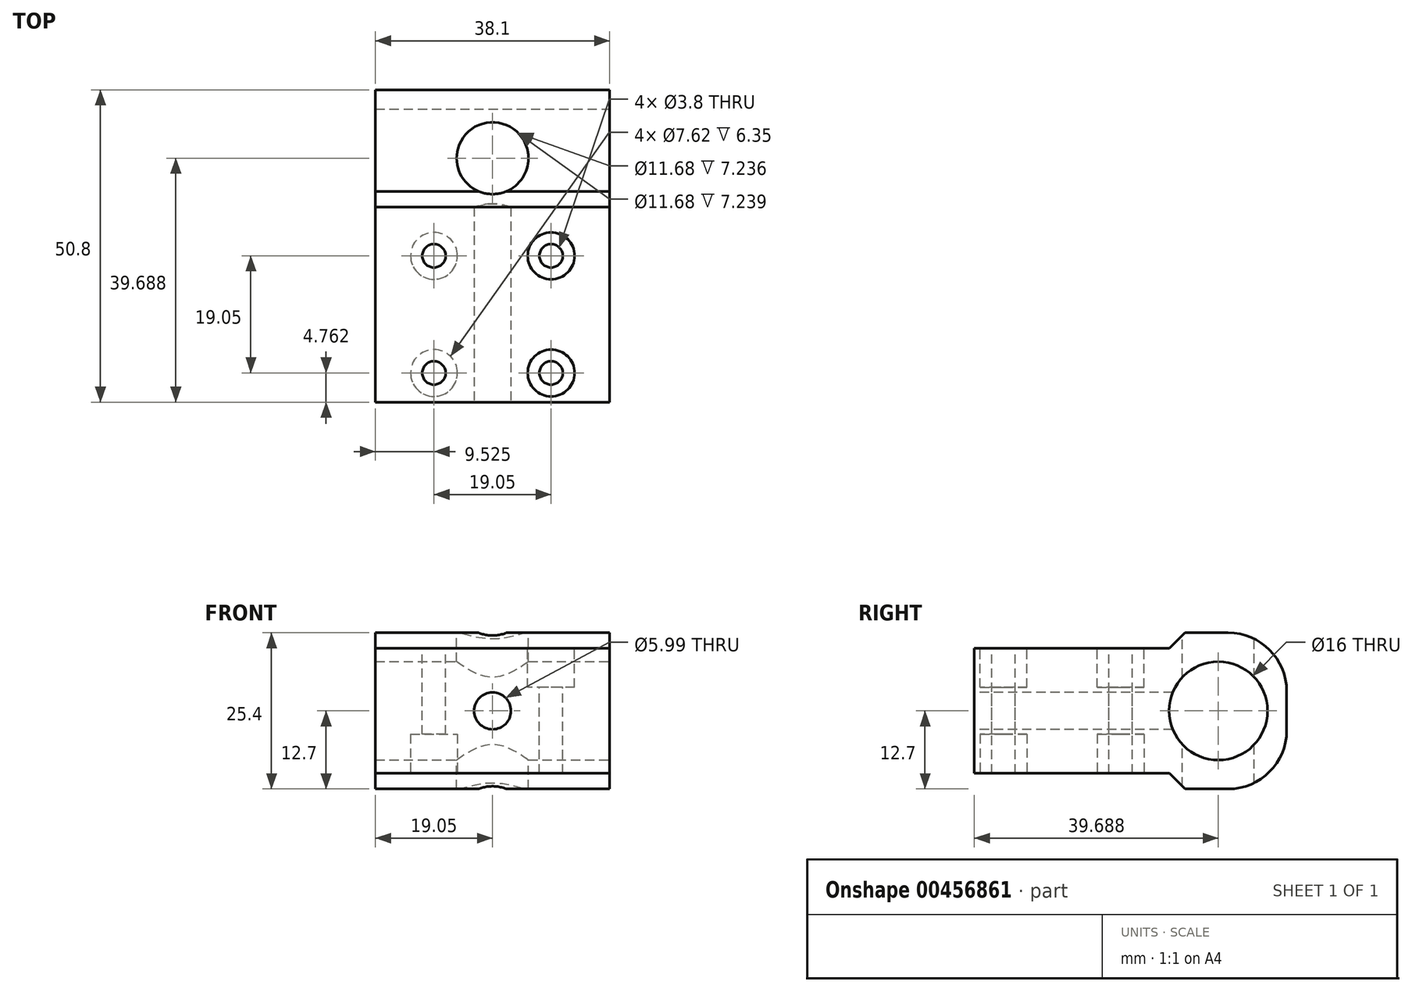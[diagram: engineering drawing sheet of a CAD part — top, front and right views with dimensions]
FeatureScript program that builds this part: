
annotation { "Feature Type Name" : "Feature", "Feature Type Description" : "" }
export const myFeature = defineFeature(function(context is Context, id is Id, definition is map)
    precondition{}
    {
        {
            var Q0;
            Q0=qCreatedBy(makeId("Top.planeOp"),FACE);
            var sketch = newSketch(context, id + "F0", { "sketchPlane" : qUnion([Q0])});
            skLineSegment(sketch, "E0.bottom", {"start": v(19.05, -25.4) * mm, "end": v(-19.05, -25.4) * mm});
            skLineSegment(sketch, "E0.top", {"start": v(19.05, 25.4) * mm, "end": v(-19.05, 25.4) * mm});
            skLineSegment(sketch, "E0.left", {"start": v(19.05, -25.4) * mm, "end": v(19.05, 25.4) * mm});
            skLineSegment(sketch, "E0.right", {"start": v(-19.05, -25.4) * mm, "end": v(-19.05, 25.4) * mm});
            skPoint(sketch, "E0.middle", {"position": v(0, 0) * mm});
            skSolve(sketch);
        }
        {
            var Q0;
            Q0 = qSketchRegion(id + "F0", true);
            extrude(context, id + "F1", {"entities" : qUnion([Q0]), "depth" : 25.4 * mm});
        }
        {
            var Q0;
            Q0=makeQuery(id+"F1.opExtrude","SWEPT_FACE",FACE,{"disambiguationData":[OSD([sQuery(id+"F0.wireOp",EDGE,"E0.left")])]});
            var sketch = newSketch(context, id + "F2", { "sketchPlane" : qUnion([Q0])});
            skCircle(sketch, "E1", {"center": v(14.29, 12.7) * mm, "radius": 8 * mm});
            skPoint(sketch, "E1.centerSnap0", {"position": v(25.4, 12.7) * mm});
            skSolve(sketch);
        }
        {
            var Q0;
            Q0 = qSketchRegion(id + "F2", true);
            extrude(context, id + "F3", {"entities" : qUnion([Q0]), "operationType" : NewBodyOperationType.REMOVE, "endBound" : BoundingType.THROUGH_ALL, "oppositeDirection" : true, "depth" : 25.4 * mm});
        }
        {
            var Q0;
            Q0=makeQuery(id+"F1.opExtrude","SWEPT_FACE",FACE,{"disambiguationData":[OSD([sQuery(id+"F0.wireOp",EDGE,"E0.bottom")])]});
            var sketch = newSketch(context, id + "F4", { "sketchPlane" : qUnion([Q0])});
            skCircle(sketch, "E2", {"center": v(0, 12.7) * mm, "radius": 3 * mm});
            skPoint(sketch, "E2.centerSnap0", {"position": v(19.05, 12.7) * mm});
            skSolve(sketch);
        }
        {
            var Q0;
            Q0 = qSketchRegion(id + "F4", true);
            extrude(context, id + "F5", {"entities" : qUnion([Q0]), "operationType" : NewBodyOperationType.REMOVE, "endBound" : BoundingType.UP_TO_NEXT, "oppositeDirection" : true, "depth" : 25.4 * mm});
        }
        {
            var Q0;
            Q0=makeQuery(id+"F1.opExtrude","CAP_EDGE",EDGE,{"disambiguationData":[OSD([sQuery(id+"F0.wireOp",EDGE,"E0.top")])],"isStart":false});
            var Q1;
            Q1=makeQuery(id+"F1.opExtrude","CAP_EDGE",EDGE,{"disambiguationData":[OSD([sQuery(id+"F0.wireOp",EDGE,"E0.top")])],"isStart":true});
            fillet(context, id + "F6", {"entities" : qUnion([Q0, Q1]), "radius" : 9.52 * mm, "tangentPropagation" : true, "allowEdgeOverflow" : false});
        }
        {
            var Q0;
            Q0=makeQuery(id+"F1.opExtrude","CAP_FACE",FACE,{"disambiguationData":[OSD([sQuery(id+"F0.wireOp",EDGE,"E0.bottom"),sQuery(id+"F0.wireOp",EDGE,"E0.top"),sQuery(id+"F0.wireOp",EDGE,"E0.left"),sQuery(id+"F0.wireOp",EDGE,"E0.right")])],"isStart":false});
            var sketch = newSketch(context, id + "F7", { "sketchPlane" : qUnion([Q0])});
            skPoint(sketch, "E3", {"position": v(-9.53, -20.64) * mm});
            skPoint(sketch, "E4", {"position": v(-9.53, -1.59) * mm});
            skPoint(sketch, "E5", {"position": v(9.52, -1.59) * mm});
            skPoint(sketch, "E6", {"position": v(9.52, -20.64) * mm});
            skSolve(sketch);
        }
        {
            var Q0;
            Q0=sQuery(id+"F7.wireOp",VERTEX,"E4");
            var Q1;
            Q1=sQuery(id+"F7.wireOp",VERTEX,"E3");
            var Q2;
            Q2=sQuery(id+"F7.wireOp",VERTEX,"E6");
            var Q3;
            Q3=sQuery(id+"F7.wireOp",VERTEX,"E5");
            var Q4;
            Q4=makeQuery(id+"F1.opExtrude","SWEPT_BODY",BODY,{"disambiguationData":[OSD([sQuery(id+"F0.wireOp",EDGE,"E0.bottom"),sQuery(id+"F0.wireOp",EDGE,"E0.top"),sQuery(id+"F0.wireOp",EDGE,"E0.left"),sQuery(id+"F0.wireOp",EDGE,"E0.right")])]});
            hole(context, id + "F8", {"style" : HoleStyle.C_SINK, "endStyle" : HoleEndStyle.THROUGH, "holeDiameter" : 3.8 * mm, "cSinkDiameter" : 4.32 * mm, "cSinkAngle" : 90 * degree, "isTappedThrough" : true, "tappedDepth" : 12.7 * mm, "tapClearance" : 3, "startFromSketch" : true, "locations" : qUnion([Q0, Q1, Q2, Q3]), "scope" : qUnion([Q4])});
        }
        {
            var Q0;
            Q0=makeQuery(id+"F1.opExtrude","CAP_FACE",FACE,{"disambiguationData":[OSD([sQuery(id+"F0.wireOp",EDGE,"E0.bottom"),sQuery(id+"F0.wireOp",EDGE,"E0.top"),sQuery(id+"F0.wireOp",EDGE,"E0.left"),sQuery(id+"F0.wireOp",EDGE,"E0.right")])],"isStart":false});
            var sketch = newSketch(context, id + "F9", { "sketchPlane" : qUnion([Q0])});
            skCircle(sketch, "E7", {"center": v(9.52, -1.59) * mm, "radius": 3.81 * mm});
            skCircle(sketch, "E8", {"center": v(9.52, -20.64) * mm, "radius": 3.81 * mm});
            skSolve(sketch);
        }
        {
            var Q0;
            Q0 = qSketchRegion(id + "F9", true);
            extrude(context, id + "F10", {"entities" : qUnion([Q0]), "operationType" : NewBodyOperationType.REMOVE, "oppositeDirection" : true, "depth" : 8.9 * mm});
        }
        {
            var Q0;
            Q0=makeQuery(id+"F1.opExtrude","CAP_FACE",FACE,{"disambiguationData":[OSD([sQuery(id+"F0.wireOp",EDGE,"E0.bottom"),sQuery(id+"F0.wireOp",EDGE,"E0.top"),sQuery(id+"F0.wireOp",EDGE,"E0.left"),sQuery(id+"F0.wireOp",EDGE,"E0.right")])],"isStart":true});
            var sketch = newSketch(context, id + "F11", { "sketchPlane" : qUnion([Q0])});
            skCircle(sketch, "E9", {"center": v(-9.53, 20.64) * mm, "radius": 3.81 * mm});
            skCircle(sketch, "E10", {"center": v(-9.53, 1.59) * mm, "radius": 3.81 * mm});
            skSolve(sketch);
        }
        {
            var Q0;
            Q0 = qSketchRegion(id + "F11", true);
            extrude(context, id + "F12", {"entities" : qUnion([Q0]), "operationType" : NewBodyOperationType.REMOVE, "oppositeDirection" : true, "depth" : 8.9 * mm});
        }
        {
            var Q0;
            Q0=makeQuery(id+"F1.opExtrude","SWEPT_FACE",FACE,{"disambiguationData":[OSD([sQuery(id+"F0.wireOp",EDGE,"E0.right")])]});
            var sketch = newSketch(context, id + "F13", { "sketchPlane" : qUnion([Q0])});
            skLineSegment(sketch, "E11", {"start": v(25.4, 25.4) * mm, "end": v(25.4, 22.86) * mm});
            skLineSegment(sketch, "E12", {"start": v(25.4, 22.86) * mm, "end": v(-6.35, 22.86) * mm});
            skLineSegment(sketch, "E13", {"start": v(-6.35, 22.86) * mm, "end": v(-8.89, 25.4) * mm});
            skLineSegment(sketch, "E14", {"start": v(-8.9, 25.4) * mm, "end": v(25.4, 25.4) * mm});
            skLineSegment(sketch, "E15", {"start": v(25.4, 0) * mm, "end": v(25.4, 2.54) * mm});
            skLineSegment(sketch, "E16", {"start": v(25.4, 2.54) * mm, "end": v(-6.35, 2.54) * mm});
            skLineSegment(sketch, "E17", {"start": v(-6.35, 2.54) * mm, "end": v(-8.89, 0) * mm});
            skLineSegment(sketch, "E18", {"start": v(-8.89, 0) * mm, "end": v(25.4, 0) * mm});
            skSolve(sketch);
        }
        {
            var Q0;
            Q0 = qSketchRegion(id + "F13", true);
            extrude(context, id + "F14", {"entities" : qUnion([Q0]), "operationType" : NewBodyOperationType.REMOVE, "endBound" : BoundingType.THROUGH_ALL, "oppositeDirection" : true, "depth" : 25.4 * mm});
        }
        {
            var Q0;
            Q0=makeQuery(id+"F1.opExtrude","CAP_FACE",FACE,{"disambiguationData":[OSD([sQuery(id+"F0.wireOp",EDGE,"E0.bottom"),sQuery(id+"F0.wireOp",EDGE,"E0.top"),sQuery(id+"F0.wireOp",EDGE,"E0.left"),sQuery(id+"F0.wireOp",EDGE,"E0.right")])],"isStart":false});
            var sketch = newSketch(context, id + "F15", { "sketchPlane" : qUnion([Q0])});
            skCircle(sketch, "E19", {"center": v(0, 14.29) * mm, "radius": 5.84 * mm});
            skPoint(sketch, "E19.centerSnap0", {"position": v(0, 8.89) * mm});
            skSolve(sketch);
        }
        {
            var Q0;
            Q0 = qSketchRegion(id + "F15", true);
            extrude(context, id + "F16", {"entities" : qUnion([Q0]), "operationType" : NewBodyOperationType.REMOVE, "endBound" : BoundingType.THROUGH_ALL, "oppositeDirection" : true, "depth" : 25.4 * mm});
        }
    });
